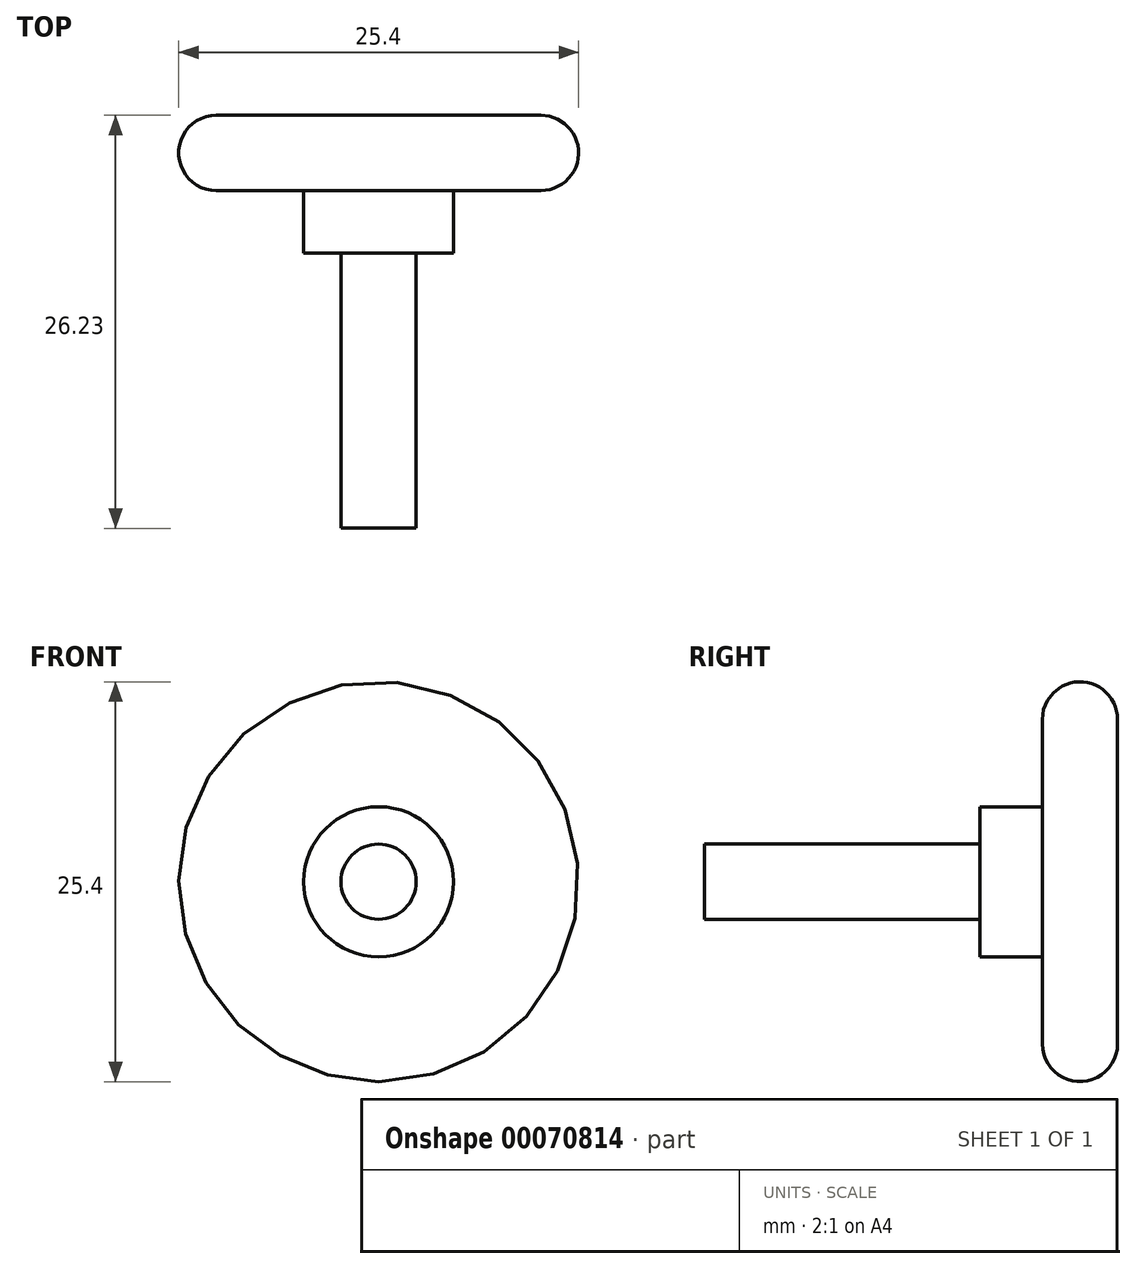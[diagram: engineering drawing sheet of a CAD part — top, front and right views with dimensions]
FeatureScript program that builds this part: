
annotation { "Feature Type Name" : "Feature", "Feature Type Description" : "" }
export const myFeature = defineFeature(function(context is Context, id is Id, definition is map)
    precondition{}
    {
        {
            var Q0;
            Q0=qCreatedBy(makeId("Front.planeOp"),FACE);
            var sketch = newSketch(context, id + "F0", { "sketchPlane" : qUnion([Q0])});
            skCircle(sketch, "E0", {"center": v(0, 0) * mm, "radius": 12.7 * mm});
            skSolve(sketch);
        }
        {
            var Q0;
            Q0 = qSketchRegion(id + "F0", true);
            extrude(context, id + "F1", {"entities" : qUnion([Q0]), "depth" : 4.78 * mm});
        }
        {
            var Q0;
            Q0=makeQuery(id+"F1.opExtrude","CAP_EDGE",EDGE,{"disambiguationData":[OSD([sQuery(id+"F0.wireOp",EDGE,"E0")])],"isStart":true});
            var Q1;
            Q1=makeQuery(id+"F1.opExtrude","CAP_EDGE",EDGE,{"disambiguationData":[OSD([sQuery(id+"F0.wireOp",EDGE,"E0")])],"isStart":false});
            fillet(context, id + "F2", {"entities" : qUnion([Q0, Q1]), "radius" : 2.4 * mm, "tangentPropagation" : true, "allowEdgeOverflow" : false});
        }
        {
            var Q0;
            Q0=makeQuery(id+"F1.opExtrude","CAP_FACE",FACE,{"disambiguationData":[OSD([sQuery(id+"F0.wireOp",EDGE,"E0")])],"isStart":false});
            var sketch = newSketch(context, id + "F3", { "sketchPlane" : qUnion([Q0])});
            skCircle(sketch, "E1", {"center": v(0, 0) * mm, "radius": 4.76 * mm});
            skSolve(sketch);
        }
        {
            var Q0;
            Q0 = qSketchRegion(id + "F3", true);
            extrude(context, id + "F4", {"entities" : qUnion([Q0]), "operationType" : NewBodyOperationType.ADD, "endBound" : BoundingType.SYMMETRIC, "depth" : 7.95 * mm});
        }
        {
            var Q0;
            Q0=makeQuery(id+"F4.opExtrude","CAP_FACE",FACE,{"disambiguationData":[OSD([sQuery(id+"F3.wireOp",EDGE,"E1")])],"isStart":false});
            var sketch = newSketch(context, id + "F5", { "sketchPlane" : qUnion([Q0])});
            skCircle(sketch, "E2", {"center": v(0, 0) * mm, "radius": 2.39 * mm});
            skSolve(sketch);
        }
        {
            var Q0;
            Q0=makeQuery(id+"F5.imprint","IMPRINT",FACE,{"disambiguationData":[TD([[makeQuery(id+"F5.imprint","IMPRINT",EDGE,{"derivedFrom":sQuery(id+"F5.wireOp",EDGE,"E2")}),1.0]])]});
            extrude(context, id + "F6", {"entities" : qUnion([Q0]), "operationType" : NewBodyOperationType.ADD, "depth" : 17.48 * mm});
        }
    });
